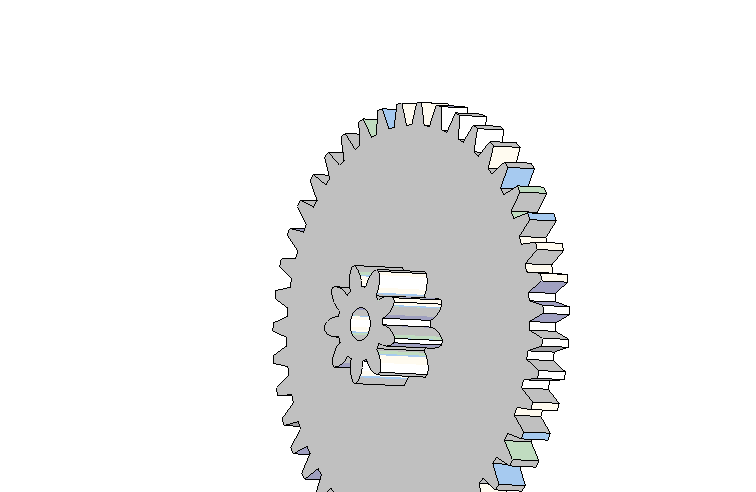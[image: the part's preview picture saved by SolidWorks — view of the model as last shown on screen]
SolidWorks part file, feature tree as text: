
SOLIDWORKS PART (.sldprt)
format: sldprt  version: not decoded by parser v0  size: 327,168 bytes
history: native  units: mm
features: plane x3, sketch x3, cut_extrude x2, pattern_circular x2, material x1, revolve x1 (+10 scaffold rows collapsed)
feature tree (22):
  scaffold x10  (default folders/planes/origin — collapsed)
  material  "Matériau <non spécifié>"
  plane  "Plan de face"
  plane  "Plan de dessus"
  plane  "Plan de droite"
  sketch  "Esquisse1"  dims[c1.D1=1.0mm c1.D2=1.8mm c1.D3=5.0mm c1.D4=6.75mm c1.D5=0.8mm c1.D6=0.2mm c1.D7=0.2mm c1.D8=3.4mm c1.D9=1.8mm c1.D10=1.1mm c1.D11=0.85mm c2.D11=135.0deg c2.D3=5.4mm c2.D6=1.3mm c2.D8=4.8mm]
  revolve  "Révolution1"  Angle=360deg
  sketch  "Esquisse2"  dims[c1.D1=2.25mm c1.D2=1.8mm c1.D7=0.8mm c1.D8=0.8mm c2.D2=~2.483695mm c3.D2=10.0deg c3.D3=~2.483695mm c4.D3=10.0deg c5.D3=0.1mm c5.D4=0.1mm c5.D5=0.55mm c5.D6=~0.861707mm c6.D6=170.0deg c7.D6=0.55mm]
  cut_extrude  "Enlèv. mat.-Extru.1"  Depth=1.8mm
  pattern_circular  "Répétition circulaire1"  Count=9 Angle=40deg
  sketch  "Esquisse3"  dims[c1.D1=0.13mm c1.D2=0.13mm c1.D3=0.4mm c2.D3=110.0deg c2.D4=0.4mm c3.D4=110.0deg c3.D5=6.07mm c3.D6=1.0mm]
  cut_extrude  "Enlèv. mat.-Extru.3"  Depth=10mm
  pattern_circular  "Répétition circulaire2"  Count=43 Angle=8.37deg
decode coverage: 8 of 8 modeling features carry decoded parameters
note: ~ marks probable driven/reference dimensions
note: suppression state not decoded; provenance and decode notes live in map.json
